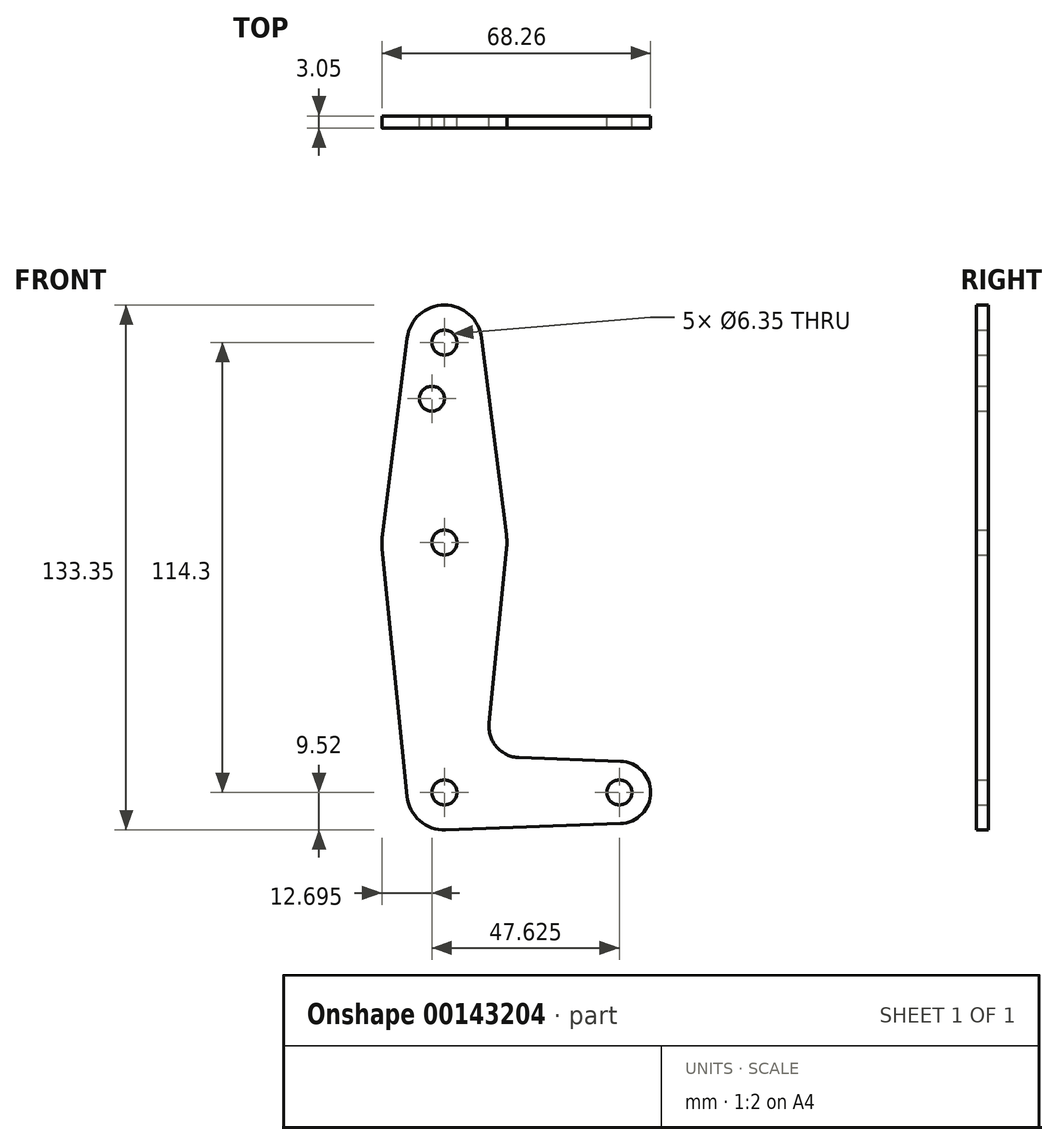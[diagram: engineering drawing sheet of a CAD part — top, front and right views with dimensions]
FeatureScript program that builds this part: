
annotation { "Feature Type Name" : "Feature", "Feature Type Description" : "" }
export const myFeature = defineFeature(function(context is Context, id is Id, definition is map)
    precondition{}
    {
        {
            var Q0;
            Q0=qCreatedBy(makeId("Front.planeOp"),FACE);
            var sketch = newSketch(context, id + "F0", { "sketchPlane" : qUnion([Q0])});
            skLineSegment(sketch, "E0", {"start": v(0, 114.3) * mm, "end": v(0, 0) * mm, "construction": true});
            skLineSegment(sketch, "E1", {"start": v(0, 0) * mm, "end": v(44.45, 0) * mm, "construction": true});
            skCircle(sketch, "E2", {"center": v(0, 114.3) * mm, "radius": 9.53 * mm});
            skCircle(sketch, "E3", {"center": v(0, 63.5) * mm, "radius": 15.88 * mm});
            skCircle(sketch, "E4", {"center": v(44.45, 0) * mm, "radius": 7.94 * mm});
            skCircle(sketch, "E5", {"center": v(0, 0) * mm, "radius": 9.53 * mm});
            skLineSegment(sketch, "E6", {"start": v(-9.45, 115.5) * mm, "end": v(-15.75, 65.48) * mm});
            skLineSegment(sketch, "E7", {"start": v(9.45, 115.5) * mm, "end": v(15.75, 65.48) * mm});
            skLineSegment(sketch, "E8", {"start": v(-15.8, 61.91) * mm, "end": v(-9.48, -0.95) * mm});
            skLineSegment(sketch, "E9", {"start": v(15.8, 61.91) * mm, "end": v(11.34, 17.6) * mm});
            skLineSegment(sketch, "E10", {"start": v(18.97, 8.85) * mm, "end": v(44.73, 7.93) * mm});
            skLineSegment(sketch, "E11", {"start": v(0.34, -9.52) * mm, "end": v(44.73, -7.93) * mm});
            skCircle(sketch, "E12", {"center": v(0, 114.3) * mm, "radius": 3.18 * mm});
            skCircle(sketch, "E13", {"center": v(-3.17, 100.03) * mm, "radius": 3.18 * mm});
            skCircle(sketch, "E14", {"center": v(0, 63.5) * mm, "radius": 3.18 * mm});
            skCircle(sketch, "E15", {"center": v(0, 0) * mm, "radius": 3.18 * mm});
            skCircle(sketch, "E16", {"center": v(44.45, 0) * mm, "radius": 3.18 * mm});
            skArc(sketch, "E17.filletArc", {"start": v(11.34, 17.6) * mm, "mid": v(13.26, 11.57) * mm, "end": v(18.97, 8.85) * mm});
            skSolve(sketch);
        }
        {
            var Q0;
            Q0 = qSketchRegion(id + "F0", true);
            extrude(context, id + "F1", {"entities" : qUnion([Q0]), "depth" : 3.05 * mm});
        }
    });
